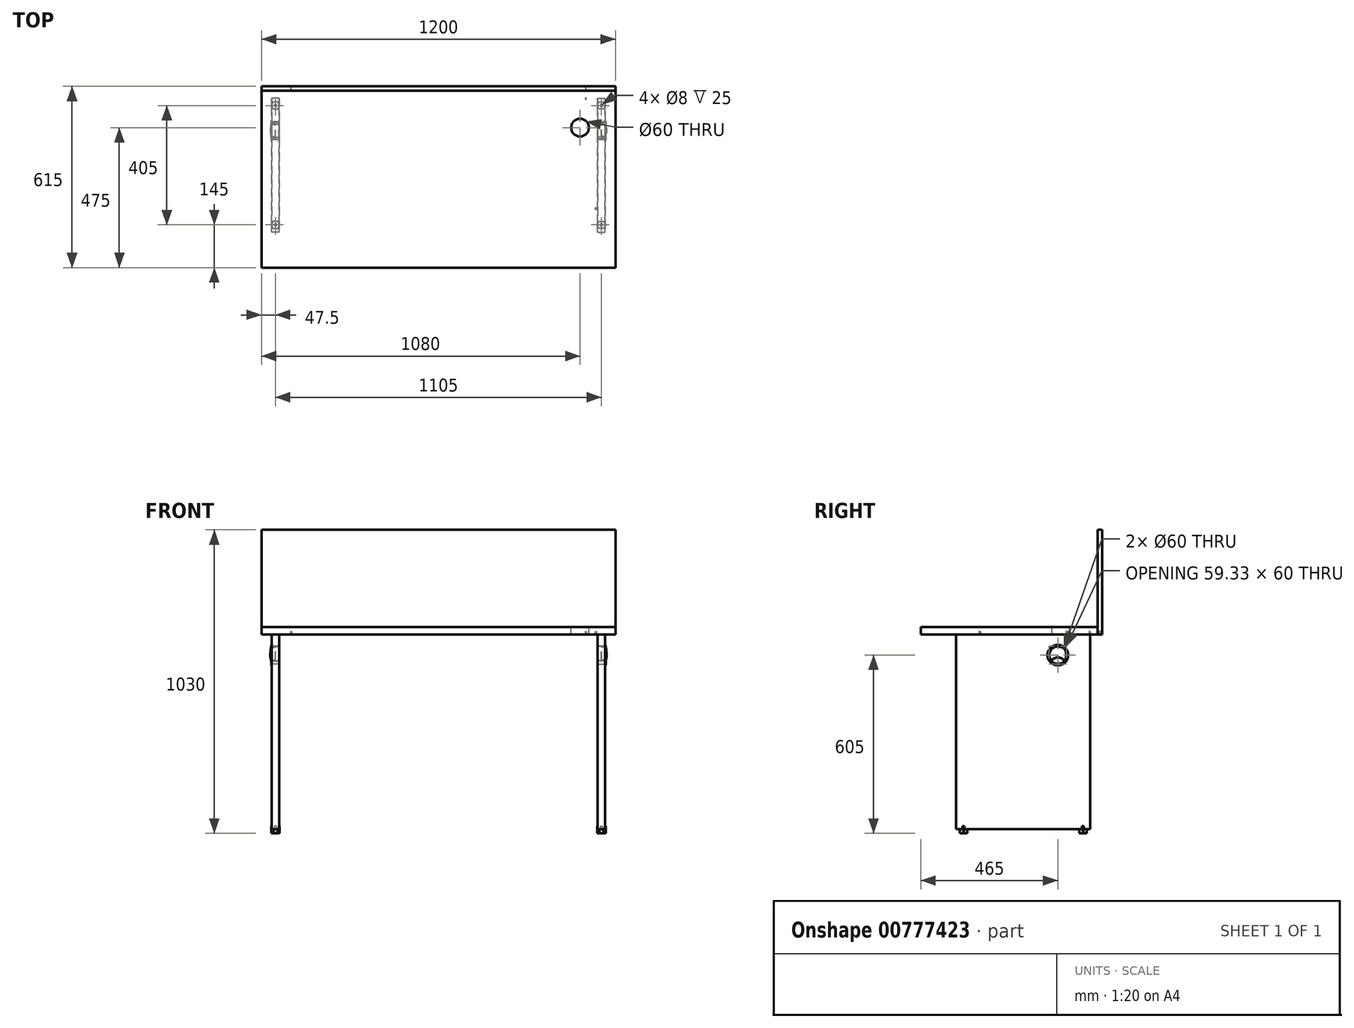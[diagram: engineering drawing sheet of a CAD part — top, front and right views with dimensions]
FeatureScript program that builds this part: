
annotation { "Feature Type Name" : "Feature", "Feature Type Description" : "" }
export const myFeature = defineFeature(function(context is Context, id is Id, definition is map)
    precondition{}
    {
        {
            assignVariable(context, id + "F0", {"name" : "GrosorMelamina", "anyValue" : 25});
        }
        {
            assignVariable(context, id + "F1", {"name" : "GrosorMelaminaDelgado", "anyValue" : 15});
        }
        {
            var Q0;
            Q0=qCreatedBy(makeId("Top.planeOp"),FACE);
            var sketch = newSketch(context, id + "F2", { "sketchPlane" : qUnion([Q0])});
            skLineSegment(sketch, "E0.bottom", {"start": v(600, 300) * mm, "end": v(-600, 300) * mm});
            skLineSegment(sketch, "E0.top", {"start": v(600, -300) * mm, "end": v(-600, -300) * mm});
            skLineSegment(sketch, "E0.left", {"start": v(600, 300) * mm, "end": v(600, -300) * mm});
            skLineSegment(sketch, "E0.right", {"start": v(-600, 300) * mm, "end": v(-600, -300) * mm});
            skPoint(sketch, "E0.middle", {"position": v(0, 0) * mm});
            skCircle(sketch, "E1", {"center": v(480, 175) * mm, "radius": 30 * mm});
            skSolve(sketch);
        }
        {
            var Q0;
            Q0 = qSketchRegion(id + "F2", true);
            extrude(context, id + "F3", {"entities" : qUnion([Q0]), "oppositeDirection" : true, "depth" : (getVariable(context, 'GrosorMelamina')) * mm, "offsetDistance" : 25 * mm});
        }
        {
            var Q0;
            Q0=makeQuery(id+"F3.opExtrude","SWEPT_FACE",FACE,{"disambiguationData":[OSD([sQuery(id+"F2.wireOp",EDGE,"E0.left")])]});
            cPlane(context, id + "F4", {"entities" : qUnion([Q0]), "cplaneType" : CPlaneType.OFFSET, "offset" : 35 * mm, "oppositeDirection" : true, "width" : 150 * mm, "height" : 150 * mm});
        }
        {
            var Q0;
            Q0=qCreatedBy(id+"F4.planeOp",FACE);
            var sketch = newSketch(context, id + "F5", { "sketchPlane" : qUnion([Q0])});
            skLineSegment(sketch, "E2.bottom", {"start": v(275, -25) * mm, "end": v(-180, -25) * mm});
            skLineSegment(sketch, "E2.top", {"start": v(275, -700) * mm, "end": v(-180, -700) * mm, "construction": true});
            skLineSegment(sketch, "E2.left", {"start": v(275, -25) * mm, "end": v(275, -685) * mm});
            skLineSegment(sketch, "E2.right", {"start": v(-180, -25) * mm, "end": v(-180, -685) * mm});
            skCircle(sketch, "E3", {"center": v(165, -95) * mm, "radius": 30 * mm});
            skLineSegment(sketch, "E4", {"start": v(-180, -685) * mm, "end": v(275, -685) * mm});
            skLineSegment(sketch, "E5", {"start": v(-180, -700) * mm, "end": v(-180, -685) * mm, "construction": true});
            skLineSegment(sketch, "E6", {"start": v(275, -700) * mm, "end": v(275, -685) * mm, "construction": true});
            skSolve(sketch);
        }
        {
            var Q0;
            Q0=qCreatedBy(makeId("Top.planeOp"),FACE);
            var Q1;
            Q1=sQuery(id+"F5.wireOp",VERTEX,"E2.top.end");
            cPlane(context, id + "F6", {"entities" : qUnion([Q0, Q1]), "cplaneType" : CPlaneType.PLANE_POINT, "offset" : 25 * mm, "width" : 150 * mm, "height" : 150 * mm});
        }
        {
            var Q0;
            Q0 = qSketchRegion(id + "F5", true);
            extrude(context, id + "F7", {"entities" : qUnion([Q0]), "oppositeDirection" : true, "depth" : (getVariable(context, 'GrosorMelamina')) * mm, "offsetDistance" : 25 * mm});
        }
        {
            var Q0;
            Q0=qCreatedBy(makeId("Front.planeOp"),FACE);
            var Q1;
            Q1=sQuery(id+"F5.wireOp",VERTEX,"E3.center");
            cPlane(context, id + "F8", {"entities" : qUnion([Q0, Q1]), "cplaneType" : CPlaneType.PLANE_POINT, "offset" : 25 * mm, "width" : 150 * mm, "height" : 150 * mm});
        }
        {
            var Q0;
            Q0=qCreatedBy(id+"F8.planeOp",FACE);
            var sketch = newSketch(context, id + "F9", { "sketchPlane" : qUnion([Q0])});
            skLineSegment(sketch, "E7", {"start": v(541, -65) * mm, "end": v(565, -65) * mm});
            skLineSegment(sketch, "E8", {"start": v(565, -65) * mm, "end": v(565, -60) * mm});
            skLineSegment(sketch, "E9", {"start": v(565, -60) * mm, "end": v(566, -60.58) * mm});
            skLineSegment(sketch, "E10", {"start": v(566, -60.58) * mm, "end": v(567, -65) * mm});
            skLineSegment(sketch, "E11", {"start": v(567, -65) * mm, "end": v(565, -67) * mm});
            skLineSegment(sketch, "E12", {"start": v(565, -67) * mm, "end": v(553, -67) * mm});
            skLineSegment(sketch, "E13", {"start": v(553, -67) * mm, "end": v(553, -66) * mm});
            skLineSegment(sketch, "E14", {"start": v(553, -66) * mm, "end": v(540, -66) * mm});
            skLineSegment(sketch, "E15", {"start": v(540, -66) * mm, "end": v(541, -65) * mm});
            skLineSegment(sketch, "E16", {"start": v(529.9, -95) * mm, "end": v(565, -95) * mm, "construction": true});
            skLineSegment(sketch, "E17", {"start": v(552, -67) * mm, "end": v(552, -68.5) * mm});
            skLineSegment(sketch, "E18", {"start": v(552, -68.5) * mm, "end": v(565.63, -68.5) * mm});
            skArc(sketch, "E19", {"start": v(567, -65) * mm, "mid": v(569.25, -79.93) * mm, "end": v(570, -95) * mm});
            skLineSegment(sketch, "E20", {"start": v(552, -67) * mm, "end": v(565, -67) * mm});
            skLineSegment(sketch, "E21", {"start": v(570, -95) * mm, "end": v(568, -95) * mm});
            skArc(sketch, "E22.trimOffspring", {"start": v(565.63, -68.5) * mm, "mid": v(567.4, -81.7) * mm, "end": v(568, -95) * mm});
            skSolve(sketch);
        }
        {
            var Q0;
            Q0=makeQuery(id+"F9.imprint","IMPRINT",FACE,{"disambiguationData":[TD([[makeQuery(id+"F9.imprint","IMPRINT",EDGE,{"derivedFrom":sQuery(id+"F9.wireOp",EDGE,"E7")}),-1.0]])]});
            var Q1;
            Q1=sQuery(id+"F9.wireOp",EDGE,"E16");
            revolve(context, id + "F10", {"surfaceOperationType" : NewSurfaceOperationType.NEW, "entities" : qUnion([Q0]), "axis" : qUnion([Q1]), "revolveType" : RevolveType.FULL});
        }
        {
            var Q0;
            {var subQ1=sQuery(id+"F9.wireOp",EDGE,"E11");Q0=makeQuery(id+"F9.imprint","IMPRINT",FACE,{"disambiguationData":[TD([[makeQuery(id+"F9.imprint","IMPRINT",EDGE,{"derivedFrom":subQ1}),1.0]])]});}
            var Q1;
            Q1=sQuery(id+"F9.wireOp",EDGE,"E16");
            revolve(context, id + "F11", {"surfaceOperationType" : NewSurfaceOperationType.NEW, "entities" : qUnion([Q0]), "axis" : qUnion([Q1]), "revolveType" : RevolveType.FULL});
        }
        {
            var Q0;
            Q0=qCreatedBy(makeId("Right.planeOp"),FACE);
            var sketch = newSketch(context, id + "F12", { "sketchPlane" : qUnion([Q0])});
            skArc(sketch, "E23", {"start": v(187.5, -114.84) * mm, "mid": v(165, -103) * mm, "end": v(142.5, -114.84) * mm});
            skCircle(sketch, "E24.0", {"center": v(165, -95) * mm, "radius": 30 * mm});
            skLineSegment(sketch, "E25", {"start": v(165, -103) * mm, "end": v(165, -65) * mm, "construction": true});
            skSolve(sketch);
        }
        {
            var Q0;
            {var subQ0=sQuery(id+"F12.wireOp",EDGE,"E23");Q0=makeQuery(id+"F12.imprint","IMPRINT",FACE,{"disambiguationData":[TD([[makeQuery(id+"F12.imprint","IMPRINT",EDGE,{"derivedFrom":subQ0}),1.0]])]});}
            extrude(context, id + "F13", {"entities" : qUnion([Q0]), "operationType" : NewBodyOperationType.REMOVE, "endBound" : BoundingType.THROUGH_ALL, "depth" : 25 * mm, "offsetDistance" : 25 * mm});
        }
        {
            var Q0;
            Q0=makeQuery(id+"F3.opExtrude","CAP_FACE",FACE,{"disambiguationData":[OSD([sQuery(id+"F2.wireOp",EDGE,"E0.bottom"),sQuery(id+"F2.wireOp",EDGE,"E0.top"),sQuery(id+"F2.wireOp",EDGE,"E0.left"),sQuery(id+"F2.wireOp",EDGE,"E0.right"),sQuery(id+"F2.wireOp",EDGE,"E1")])],"isStart":false});
            var sketch = newSketch(context, id + "F14", { "sketchPlane" : qUnion([Q0])});
            skLineSegment(sketch, "E26", {"start": v(533.5, 100) * mm, "end": v(533.5, -195) * mm, "construction": true});
            skCircle(sketch, "E27", {"center": v(533.5, 100) * mm, "radius": 2.5 * mm});
            skCircle(sketch, "E28", {"center": v(533.5, -195) * mm, "radius": 2.5 * mm});
            skLineSegment(sketch, "E29", {"start": v(0, -273) * mm, "end": v(500, -273) * mm, "construction": true});
            skPoint(sketch, "E29.startSnap0", {"position": v(0, -300) * mm});
            skCircle(sketch, "E30", {"center": v(500, -273) * mm, "radius": 2 * mm});
            skSolve(sketch);
        }
        {
            var Q0;
            Q0 = qSketchRegion(id + "F14", true);
            extrude(context, id + "F15", {"entities" : qUnion([Q0]), "operationType" : NewBodyOperationType.REMOVE, "oppositeDirection" : true, "depth" : 10 * mm, "offsetDistance" : 25 * mm});
        }
        {
            var Q0;
            Q0=makeQuery(id+"F7.opExtrude","SWEPT_FACE",FACE,{"disambiguationData":[OSD([sQuery(id+"F5.wireOp",EDGE,"E4")])]});
            var sketch = newSketch(context, id + "F16", { "sketchPlane" : qUnion([Q0])});
            skLineSegment(sketch, "E31", {"start": v(552.5, 180) * mm, "end": v(552.5, 155) * mm, "construction": true});
            skLineSegment(sketch, "E32", {"start": v(552.5, 155) * mm, "end": v(552.5, -250) * mm, "construction": true});
            skLineSegment(sketch, "E33", {"start": v(552.5, -250) * mm, "end": v(552.5, -275) * mm, "construction": true});
            skCircle(sketch, "E34", {"center": v(552.5, 155) * mm, "radius": 4 * mm});
            skCircle(sketch, "E35", {"center": v(552.5, -250) * mm, "radius": 4 * mm});
            skSolve(sketch);
        }
        {
            var Q0;
            Q0 = qSketchRegion(id + "F16", true);
            extrude(context, id + "F17", {"entities" : qUnion([Q0]), "operationType" : NewBodyOperationType.REMOVE, "oppositeDirection" : true, "depth" : 10 * mm, "offsetDistance" : 25 * mm});
        }
        {
            var Q0;
            Q0=qCreatedBy(id+"F6.planeOp",FACE);
            var sketch = newSketch(context, id + "F18", { "sketchPlane" : qUnion([Q0])});
            skCircle(sketch, "E36.cCircle", {"center": v(552.5, -155) * mm, "radius": 12.5 * mm, "construction": true});
            skLineSegment(sketch, "E36.0", {"start": v(559.72, -142.5) * mm, "end": v(566.93, -155) * mm});
            skLineSegment(sketch, "E36.1", {"start": v(566.93, -155) * mm, "end": v(559.72, -167.5) * mm});
            skLineSegment(sketch, "E36.2", {"start": v(559.72, -167.5) * mm, "end": v(545.28, -167.5) * mm});
            skLineSegment(sketch, "E36.3", {"start": v(545.28, -167.5) * mm, "end": v(538.07, -155) * mm});
            skLineSegment(sketch, "E36.4", {"start": v(538.07, -155) * mm, "end": v(545.28, -142.5) * mm});
            skLineSegment(sketch, "E36.5", {"start": v(545.28, -142.5) * mm, "end": v(559.72, -142.5) * mm});
            skPoint(sketch, "E36.0.midPoint", {"position": v(563.33, -148.75) * mm});
            skCircle(sketch, "E37.cCircle", {"center": v(552.5, 250) * mm, "radius": 12.5 * mm, "construction": true});
            skLineSegment(sketch, "E37.0", {"start": v(559.72, 262.5) * mm, "end": v(566.93, 250) * mm});
            skLineSegment(sketch, "E37.1", {"start": v(566.93, 250) * mm, "end": v(559.72, 237.5) * mm});
            skLineSegment(sketch, "E37.2", {"start": v(559.72, 237.5) * mm, "end": v(545.28, 237.5) * mm});
            skLineSegment(sketch, "E37.3", {"start": v(545.28, 237.5) * mm, "end": v(538.07, 250) * mm});
            skLineSegment(sketch, "E37.4", {"start": v(538.07, 250) * mm, "end": v(545.28, 262.5) * mm});
            skLineSegment(sketch, "E37.5", {"start": v(545.28, 262.5) * mm, "end": v(559.72, 262.5) * mm});
            skPoint(sketch, "E37.0.midPoint", {"position": v(563.33, 256.25) * mm});
            skCircle(sketch, "E38.0", {"center": v(552.5, -155) * mm, "radius": 4 * mm});
            skCircle(sketch, "E39.0", {"center": v(552.5, 250) * mm, "radius": 4 * mm});
            skSolve(sketch);
        }
        {
            var Q0;
            Q0 = qSketchRegion(id + "F18", true);
            var Q1;
            Q1=makeQuery(id+"F18.imprint","IMPRINT",FACE,{"disambiguationData":[TD([[makeQuery(id+"F18.imprint","IMPRINT",EDGE,{"derivedFrom":sQuery(id+"F18.wireOp",EDGE,"E38.0")}),-1.0]])]});
            var Q2;
            Q2=makeQuery(id+"F18.imprint","IMPRINT",FACE,{"disambiguationData":[TD([[makeQuery(id+"F18.imprint","IMPRINT",EDGE,{"derivedFrom":sQuery(id+"F18.wireOp",EDGE,"E39.0")}),-1.0]])]});
            extrude(context, id + "F19", {"entities" : qUnion([Q0, Q1, Q2]), "depth" : 5 * mm, "offsetDistance" : 25 * mm});
        }
        {
            var Q0;
            Q0=makeQuery(id+"F18.imprint","IMPRINT",FACE,{"disambiguationData":[TD([[makeQuery(id+"F18.imprint","IMPRINT",EDGE,{"derivedFrom":sQuery(id+"F18.wireOp",EDGE,"E39.0")}),-1.0]])]});
            var Q1;
            Q1=makeQuery(id+"F18.imprint","IMPRINT",FACE,{"disambiguationData":[TD([[makeQuery(id+"F18.imprint","IMPRINT",EDGE,{"derivedFrom":sQuery(id+"F18.wireOp",EDGE,"E38.0")}),-1.0]])]});
            extrude(context, id + "F20", {"entities" : qUnion([Q0, Q1]), "operationType" : NewBodyOperationType.ADD, "depth" : 25 * mm, "offsetDistance" : 25 * mm});
        }
        {
            var Q0;
            Q0=makeQuery(id+"F10.opRevolve","SWEPT_BODY",BODY,{"disambiguationData":[OSD([sQuery(id+"F9.wireOp",EDGE,"E7"),sQuery(id+"F9.wireOp",EDGE,"E8"),sQuery(id+"F9.wireOp",EDGE,"E9"),sQuery(id+"F9.wireOp",EDGE,"E10"),sQuery(id+"F9.wireOp",EDGE,"E11"),sQuery(id+"F9.wireOp",EDGE,"E13"),sQuery(id+"F9.wireOp",EDGE,"E14"),sQuery(id+"F9.wireOp",EDGE,"E15"),sQuery(id+"F9.wireOp",EDGE,"E20")])]});
            var Q1;
            Q1=makeQuery(id+"F7.opExtrude","SWEPT_BODY",BODY,{"disambiguationData":[OSD([sQuery(id+"F5.wireOp",EDGE,"E2.bottom"),sQuery(id+"F5.wireOp",EDGE,"E2.left"),sQuery(id+"F5.wireOp",EDGE,"E2.right"),sQuery(id+"F5.wireOp",EDGE,"E3"),sQuery(id+"F5.wireOp",EDGE,"E4")])]});
            var Q2;
            Q2=makeQuery(id+"F11.opRevolve","SWEPT_BODY",BODY,{"disambiguationData":[OSD([sQuery(id+"F9.wireOp",EDGE,"E11"),sQuery(id+"F9.wireOp",EDGE,"E17"),sQuery(id+"F9.wireOp",EDGE,"E18"),sQuery(id+"F9.wireOp",EDGE,"E19"),sQuery(id+"F9.wireOp",EDGE,"E20"),sQuery(id+"F9.wireOp",EDGE,"E21"),sQuery(id+"F9.wireOp",EDGE,"E22.trimOffspring")])]});
            var Q3;
            Q3=makeQuery(id+"F19.opExtrude","SWEPT_BODY",BODY,{"disambiguationData":[OSD([sQuery(id+"F18.wireOp",EDGE,"E37.0"),sQuery(id+"F18.wireOp",EDGE,"E37.1"),sQuery(id+"F18.wireOp",EDGE,"E37.2"),sQuery(id+"F18.wireOp",EDGE,"E37.3"),sQuery(id+"F18.wireOp",EDGE,"E37.4"),sQuery(id+"F18.wireOp",EDGE,"E37.5")])]});
            var Q4;
            Q4=makeQuery(id+"F19.opExtrude","SWEPT_BODY",BODY,{"disambiguationData":[OSD([sQuery(id+"F18.wireOp",EDGE,"E36.0"),sQuery(id+"F18.wireOp",EDGE,"E36.1"),sQuery(id+"F18.wireOp",EDGE,"E36.2"),sQuery(id+"F18.wireOp",EDGE,"E36.3"),sQuery(id+"F18.wireOp",EDGE,"E36.4"),sQuery(id+"F18.wireOp",EDGE,"E36.5")])]});
            var Q5;
            Q5=qCreatedBy(makeId("Right.planeOp"),FACE);
            mirror(context, id + "F21", {"entities" : qUnion([Q0, Q1, Q2, Q3, Q4]), "mirrorPlane" : qUnion([Q5])});
        }
        {
            var Q0;
            Q0=makeQuery(id+"F3.opExtrude","SWEPT_FACE",FACE,{"disambiguationData":[OSD([sQuery(id+"F2.wireOp",EDGE,"E0.bottom")])]});
            var sketch = newSketch(context, id + "F22", { "sketchPlane" : qUnion([Q0])});
            skLineSegment(sketch, "E40.bottom", {"start": v(-600, -25) * mm, "end": v(600, -25) * mm});
            skLineSegment(sketch, "E40.top", {"start": v(-600, 330) * mm, "end": v(600, 330) * mm});
            skLineSegment(sketch, "E40.left", {"start": v(-600, -25) * mm, "end": v(-600, 330) * mm});
            skLineSegment(sketch, "E40.right", {"start": v(600, -25) * mm, "end": v(600, 330) * mm});
            skSolve(sketch);
        }
        {
            var Q0;
            Q0 = qSketchRegion(id + "F22", true);
            extrude(context, id + "F23", {"entities" : qUnion([Q0]), "depth" : (getVariable(context, 'GrosorMelaminaDelgado')) * mm, "offsetDistance" : 25 * mm});
        }
        {
            var Q0;
            Q0=makeQuery(id+"F23.opExtrude","SWEPT_FACE",FACE,{"disambiguationData":[OSD([sQuery(id+"F22.wireOp",EDGE,"E40.bottom")])]});
            var sketch = newSketch(context, id + "F24", { "sketchPlane" : qUnion([Q0])});
            skLineSegment(sketch, "E41", {"start": v(-600, -307.5) * mm, "end": v(-500, -307.5) * mm, "construction": true});
            skLineSegment(sketch, "E42", {"start": v(-500, -307.5) * mm, "end": v(500, -307.5) * mm, "construction": true});
            skLineSegment(sketch, "E43", {"start": v(500, -307.5) * mm, "end": v(600, -307.5) * mm, "construction": true});
            skLineSegment(sketch, "E44", {"start": v(500, -307.5) * mm, "end": v(500, -273) * mm});
            skLineSegment(sketch, "E45", {"start": v(-500, -307.5) * mm, "end": v(-500, -273) * mm, "construction": true});
            skCircle(sketch, "E46", {"center": v(-500, -307.5) * mm, "radius": 2 * mm});
            skCircle(sketch, "E47", {"center": v(500, -307.5) * mm, "radius": 2 * mm});
            skSolve(sketch);
        }
        {
            var Q0;
            Q0 = qSketchRegion(id + "F24", true);
            extrude(context, id + "F25", {"entities" : qUnion([Q0]), "operationType" : NewBodyOperationType.REMOVE, "oppositeDirection" : true, "depth" : 10 * mm, "offsetDistance" : 25 * mm});
        }
    });
